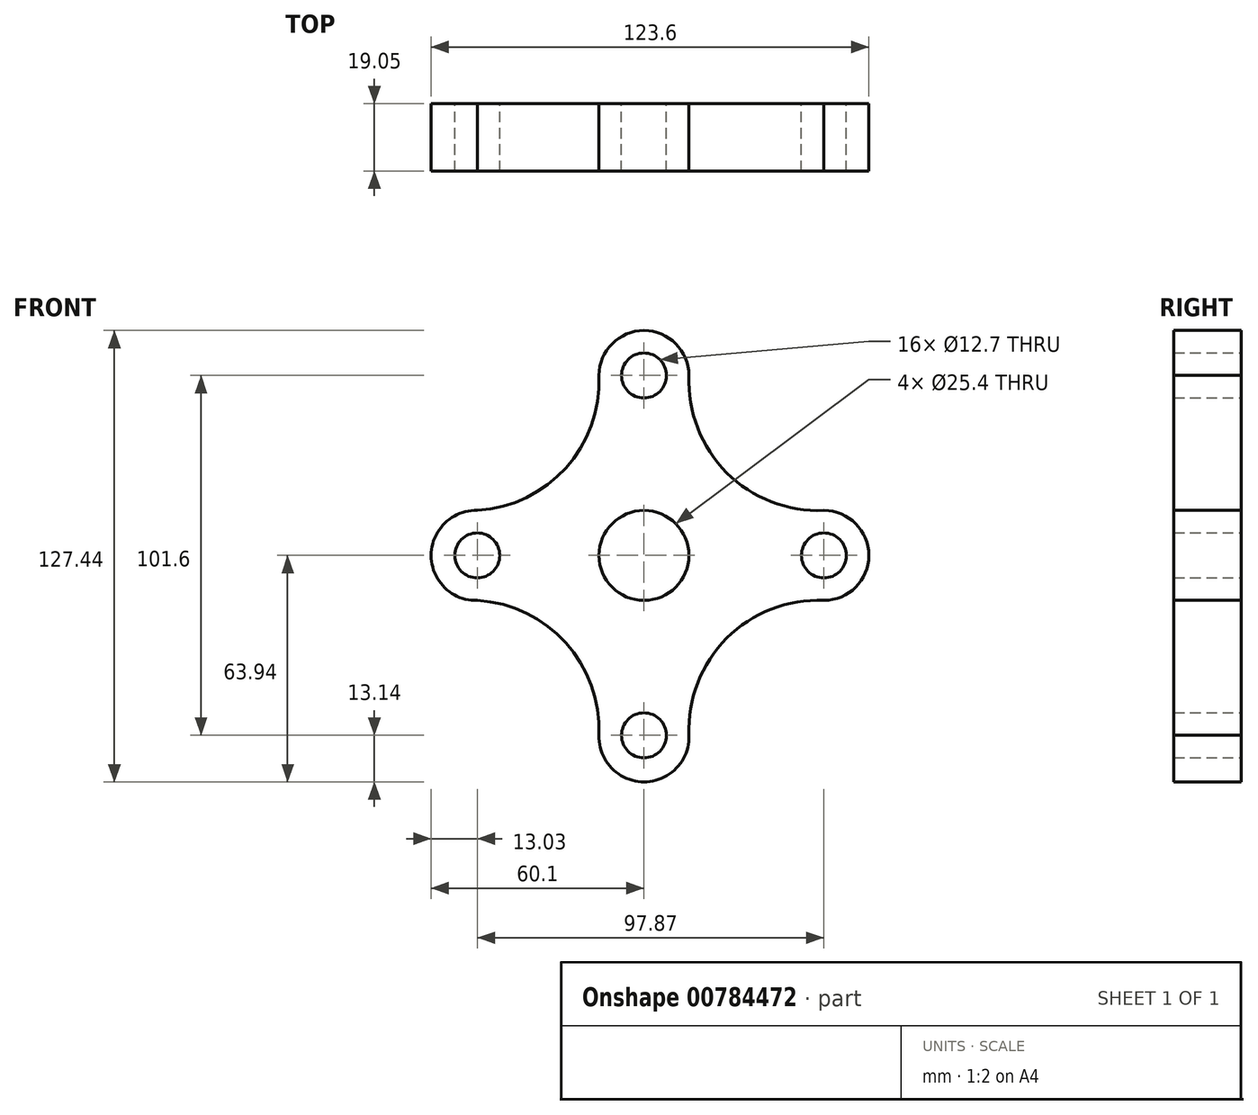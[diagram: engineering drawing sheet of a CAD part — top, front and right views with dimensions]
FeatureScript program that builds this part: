
annotation { "Feature Type Name" : "Feature", "Feature Type Description" : "" }
export const myFeature = defineFeature(function(context is Context, id is Id, definition is map)
    precondition{}
    {
        {
            var Q0;
            Q0=qCreatedBy(makeId("Front.planeOp"),FACE);
            var sketch = newSketch(context, id + "F0", { "sketchPlane" : qUnion([Q0])});
            skCircle(sketch, "E0", {"center": v(0, 0) * mm, "radius": 12.7 * mm});
            skCircle(sketch, "E1", {"center": v(0, 50.8) * mm, "radius": 6.35 * mm});
            skCircle(sketch, "E2", {"center": v(50.8, 0) * mm, "radius": 6.35 * mm});
            skCircle(sketch, "E3", {"center": v(0, -50.8) * mm, "radius": 6.35 * mm});
            skCircle(sketch, "E4", {"center": v(-47.07, 0) * mm, "radius": 6.35 * mm});
            skArc(sketch, "E5", {"start": v(12.7, 50.8) * mm, "mid": v(23.36, 23.36) * mm, "end": v(50.8, 12.7) * mm});
            skArc(sketch, "E6", {"start": v(-47.07, 12.7) * mm, "mid": v(-22.06, 24.7) * mm, "end": v(-12.7, 50.8) * mm});
            skArc(sketch, "E7", {"start": v(-12.7, -50.8) * mm, "mid": v(-22.06, -24.7) * mm, "end": v(-47.07, -12.7) * mm});
            skArc(sketch, "E8", {"start": v(50.8, -12.7) * mm, "mid": v(23.36, -23.36) * mm, "end": v(12.7, -50.8) * mm});
            skArc(sketch, "E9", {"start": v(-47.07, 12.7) * mm, "mid": v(-60.1, 0) * mm, "end": v(-47.07, -12.7) * mm});
            skArc(sketch, "E10", {"start": v(12.7, 50.8) * mm, "mid": v(0, 63.5) * mm, "end": v(-12.7, 50.8) * mm});
            skArc(sketch, "E11", {"start": v(50.8, -12.7) * mm, "mid": v(63.5, 0) * mm, "end": v(50.8, 12.7) * mm});
            skArc(sketch, "E12", {"start": v(-12.7, -50.8) * mm, "mid": v(0, -63.94) * mm, "end": v(12.7, -50.8) * mm});
            skPoint(sketch, "E13.end.orphan", {"position": v(50.8, 4.68) * mm});
            skLineSegment(sketch, "E14", {"start": v(-47.07, 0) * mm, "end": v(-47.4, 0) * mm});
            skSolve(sketch);
        }
        {
            var Q0;
            Q0 = qSketchRegion(id + "F0", true);
            extrude(context, id + "F1", {"entities" : qUnion([Q0]), "depth" : 19.05 * mm, "offsetDistance" : 25.4 * mm});
        }
    });
